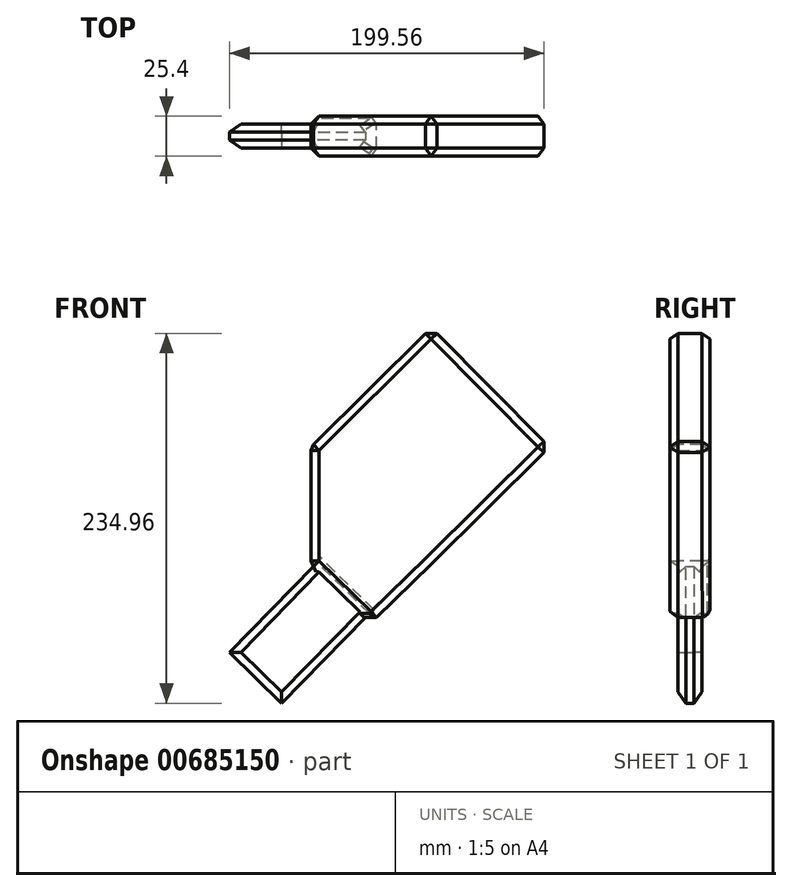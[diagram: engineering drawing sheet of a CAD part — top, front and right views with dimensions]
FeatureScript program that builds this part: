
annotation { "Feature Type Name" : "Feature", "Feature Type Description" : "" }
export const myFeature = defineFeature(function(context is Context, id is Id, definition is map)
    precondition{}
    {
        {
            var Q0;
            Q0=qCreatedBy(makeId("Front.planeOp"),FACE);
            var sketch = newSketch(context, id + "F0", { "sketchPlane" : qUnion([Q0])});
            skLineSegment(sketch, "E0", {"start": v(-76.34, 0) * mm, "end": v(0, 75.72) * mm});
            skLineSegment(sketch, "E1", {"start": v(0, 75.72) * mm, "end": v(75.1, 0) * mm});
            skLineSegment(sketch, "E2", {"start": v(75.1, 0) * mm, "end": v(0, -74.5) * mm});
            skLineSegment(sketch, "E3", {"start": v(0, -74.5) * mm, "end": v(-76.34, 0) * mm});
            skLineSegment(sketch, "E4", {"start": v(-76.34, 0) * mm, "end": v(-76.34, -74.5) * mm});
            skLineSegment(sketch, "E5", {"start": v(-76.34, -74.5) * mm, "end": v(-38.17, -111.74) * mm});
            skPoint(sketch, "E5.endSnap0", {"position": v(-38.17, -37.25) * mm});
            skLineSegment(sketch, "E6", {"start": v(-38.17, -111.74) * mm, "end": v(0, -74.5) * mm});
            skSolve(sketch);
        }
        {
            var Q0;
            Q0=makeQuery(id+"F0.imprint","IMPRINT",FACE,{"disambiguationData":[TD([[makeQuery(id+"F0.imprint","IMPRINT",EDGE,{"derivedFrom":sQuery(id+"F0.wireOp",EDGE,"E0")}),-1.0]])]});
            var Q1;
            Q1=makeQuery(id+"F0.imprint","IMPRINT",FACE,{"disambiguationData":[TD([[makeQuery(id+"F0.imprint","IMPRINT",EDGE,{"derivedFrom":sQuery(id+"F0.wireOp",EDGE,"E3")}),1.0]])]});
            extrude(context, id + "F1", {"entities" : qUnion([Q0, Q1]), "depth" : 25.4 * mm, "offsetDistance" : 25.4 * mm});
        }
        {
            var Q0;
            Q0=makeQuery(id+"F1.opExtrude","CAP_EDGE",EDGE,{"disambiguationData":[OSD([sQuery(id+"F0.wireOp",EDGE,"E2")])],"isStart":false});
            var Q1;
            Q1=makeQuery(id+"F1.opExtrude","CAP_EDGE",EDGE,{"disambiguationData":[OSD([sQuery(id+"F0.wireOp",EDGE,"E5")])],"isStart":false});
            var Q2;
            Q2=makeQuery(id+"F1.opExtrude","CAP_EDGE",EDGE,{"disambiguationData":[OSD([sQuery(id+"F0.wireOp",EDGE,"E4")])],"isStart":false});
            var Q3;
            Q3=makeQuery(id+"F1.opExtrude","CAP_FACE",FACE,{"disambiguationData":[OSD([sQuery(id+"F0.wireOp",EDGE,"E0"),sQuery(id+"F0.wireOp",EDGE,"E1"),sQuery(id+"F0.wireOp",EDGE,"E2"),sQuery(id+"F0.wireOp",EDGE,"E4"),sQuery(id+"F0.wireOp",EDGE,"E5"),sQuery(id+"F0.wireOp",EDGE,"E6")])],"isStart":false});
            var Q4;
            Q4=makeQuery(id+"F1.opExtrude","CAP_EDGE",EDGE,{"disambiguationData":[OSD([sQuery(id+"F0.wireOp",EDGE,"E2")])],"isStart":true});
            var Q5;
            Q5=makeQuery(id+"F1.opExtrude","CAP_EDGE",EDGE,{"disambiguationData":[OSD([sQuery(id+"F0.wireOp",EDGE,"E1")])],"isStart":true});
            var Q6;
            Q6=makeQuery(id+"F1.opExtrude","SWEPT_EDGE",EDGE,{"disambiguationData":[OSD([sQuery(id+"F0.wireOp",EDGE,"E1"),sQuery(id+"F0.wireOp",EDGE,"E2")])]});
            var Q7;
            Q7=makeQuery(id+"F1.opExtrude","SWEPT_EDGE",EDGE,{"disambiguationData":[OSD([sQuery(id+"F0.wireOp",EDGE,"E0"),sQuery(id+"F0.wireOp",EDGE,"E1")])]});
            var Q8;
            Q8=makeQuery(id+"F1.opExtrude","SWEPT_EDGE",EDGE,{"disambiguationData":[OSD([sQuery(id+"F0.wireOp",EDGE,"E5"),sQuery(id+"F0.wireOp",EDGE,"E6")])]});
            var Q9;
            Q9=makeQuery(id+"F1.opExtrude","SWEPT_EDGE",EDGE,{"disambiguationData":[OSD([sQuery(id+"F0.wireOp",EDGE,"E4"),sQuery(id+"F0.wireOp",EDGE,"E5")])]});
            var Q10;
            Q10=makeQuery(id+"F1.opExtrude","SWEPT_EDGE",EDGE,{"disambiguationData":[OSD([sQuery(id+"F0.wireOp",EDGE,"E0"),sQuery(id+"F0.wireOp",EDGE,"E3"),sQuery(id+"F0.wireOp",EDGE,"E4")])]});
            var Q11;
            Q11=makeQuery(id+"F1.opExtrude","CAP_EDGE",EDGE,{"disambiguationData":[OSD([sQuery(id+"F0.wireOp",EDGE,"E4")])],"isStart":true});
            var Q12;
            Q12=makeQuery(id+"F1.opExtrude","CAP_EDGE",EDGE,{"disambiguationData":[OSD([sQuery(id+"F0.wireOp",EDGE,"E5")])],"isStart":true});
            var Q13;
            Q13=makeQuery(id+"F1.opExtrude","CAP_EDGE",EDGE,{"disambiguationData":[OSD([sQuery(id+"F0.wireOp",EDGE,"E0")])],"isStart":true});
            chamfer(context, id + "F2", {"entities" : qUnion([Q0, Q1, Q2, Q3, Q4, Q5, Q6, Q7, Q8, Q9, Q10, Q11, Q12, Q13]), "width" : 5.08 * mm, "tangentPropagation" : true});
        }
        {
            var Q0;
            Q0=makeQuery(id+"F1.opExtrude","SWEPT_FACE",FACE,{"disambiguationData":[OSD([sQuery(id+"F0.wireOp",EDGE,"E5")])]});
            extrude(context, id + "F3", {"entities" : qUnion([Q0]), "operationType" : NewBodyOperationType.ADD, "depth" : 76.2 * mm, "offsetDistance" : 25.4 * mm});
        }
        {
            var Q0;
            {var subQ0=sQuery(id+"F0.wireOp",EDGE,"E5");var subQ1=sQuery(id+"F0.wireOp",EDGE,"E6");Q0=makeQuery(id+"F3.opExtrude","SWEPT_EDGE",EDGE,{"disambiguationData":[OSD([subQ0,subQ1]),TDD([makeQuery(id+"F2.opChamfer","BLEND_VERTEX",VERTEX,{"blendedFrom":[makeQuery(id+"F1.opExtrude","CAP_VERTEX",VERTEX,{"disambiguationData":[OSD([subQ0,subQ1])],"isStart":false}),makeQuery(id+"F1.opExtrude","SWEPT_EDGE",EDGE,{"disambiguationData":[OSD([subQ0,subQ1])]}),makeQuery(id+"F1.opExtrude","CAP_EDGE",EDGE,{"disambiguationData":[OSD([subQ0])],"isStart":false}),makeQuery(id+"F1.opExtrude","SWEPT_FACE",FACE,{"disambiguationData":[OSD([subQ0])]})],"blendedInto":[makeQuery(id+"F1.opExtrude","SWEPT_FACE",FACE,{"disambiguationData":[OSD([subQ0])]})]})])]});}
            var Q1;
            {var subQ0=sQuery(id+"F0.wireOp",EDGE,"E5");var subQ1=sQuery(id+"F0.wireOp",EDGE,"E6");Q1=makeQuery(id+"F3.opExtrude","SWEPT_EDGE",EDGE,{"disambiguationData":[OSD([subQ0,subQ1]),TDD([makeQuery(id+"F2.opChamfer","BLEND_VERTEX",VERTEX,{"blendedFrom":[makeQuery(id+"F1.opExtrude","SWEPT_EDGE",EDGE,{"disambiguationData":[OSD([subQ0,subQ1])]}),makeQuery(id+"F1.opExtrude","CAP_EDGE",EDGE,{"disambiguationData":[OSD([subQ0])],"isStart":true}),makeQuery(id+"F1.opExtrude","SWEPT_FACE",FACE,{"disambiguationData":[OSD([subQ0])]})],"blendedInto":[makeQuery(id+"F1.opExtrude","SWEPT_FACE",FACE,{"disambiguationData":[OSD([subQ0])]})]})])]});}
            var Q2;
            {var subQ0=sQuery(id+"F0.wireOp",EDGE,"E5");Q2=makeQuery(id+"F2.opChamfer","BLEND_EDGE",EDGE,{"blendedFrom":[makeQuery(id+"F1.opExtrude","CAP_EDGE",EDGE,{"disambiguationData":[OSD([subQ0])],"isStart":true}),makeQuery(id+"F1.opExtrude","CAP_FACE",FACE,{"disambiguationData":[OSD([sQuery(id+"F0.wireOp",EDGE,"E0"),sQuery(id+"F0.wireOp",EDGE,"E1"),sQuery(id+"F0.wireOp",EDGE,"E2"),sQuery(id+"F0.wireOp",EDGE,"E4"),subQ0,sQuery(id+"F0.wireOp",EDGE,"E6")])],"isStart":true})],"blendedInto":[makeQuery(id+"F1.opExtrude","CAP_FACE",FACE,{"disambiguationData":[OSD([sQuery(id+"F0.wireOp",EDGE,"E0"),sQuery(id+"F0.wireOp",EDGE,"E1"),sQuery(id+"F0.wireOp",EDGE,"E2"),sQuery(id+"F0.wireOp",EDGE,"E4"),subQ0,sQuery(id+"F0.wireOp",EDGE,"E6")])],"isStart":true})]});}
            var Q3;
            {var subQ0=sQuery(id+"F0.wireOp",EDGE,"E5");Q3=makeQuery(id+"F3.opExtrude","CAP_EDGE",EDGE,{"disambiguationData":[OSD([subQ0]),TDD([makeQuery(id+"F2.opChamfer","BLEND_EDGE",EDGE,{"blendedFrom":[makeQuery(id+"F1.opExtrude","CAP_EDGE",EDGE,{"disambiguationData":[OSD([subQ0])],"isStart":false}),makeQuery(id+"F1.opExtrude","SWEPT_FACE",FACE,{"disambiguationData":[OSD([subQ0])]})],"blendedInto":[makeQuery(id+"F1.opExtrude","SWEPT_FACE",FACE,{"disambiguationData":[OSD([subQ0])]})]})])],"isStart":false});}
            var Q4;
            {var subQ0=sQuery(id+"F0.wireOp",EDGE,"E5");var subQ1=sQuery(id+"F0.wireOp",EDGE,"E4");Q4=makeQuery(id+"F3.opExtrude","SWEPT_EDGE",EDGE,{"disambiguationData":[OSD([subQ1,subQ0]),TDD([makeQuery(id+"F2.opChamfer","BLEND_VERTEX",VERTEX,{"blendedFrom":[makeQuery(id+"F1.opExtrude","CAP_VERTEX",VERTEX,{"disambiguationData":[OSD([subQ1,subQ0])],"isStart":true}),makeQuery(id+"F1.opExtrude","SWEPT_EDGE",EDGE,{"disambiguationData":[OSD([subQ1,subQ0])]}),makeQuery(id+"F1.opExtrude","CAP_EDGE",EDGE,{"disambiguationData":[OSD([subQ0])],"isStart":true}),makeQuery(id+"F1.opExtrude","SWEPT_FACE",FACE,{"disambiguationData":[OSD([subQ0])]})],"blendedInto":[makeQuery(id+"F1.opExtrude","SWEPT_FACE",FACE,{"disambiguationData":[OSD([subQ0])]})]})])]});}
            var Q5;
            {var subQ0=sQuery(id+"F0.wireOp",EDGE,"E5");var subQ1=sQuery(id+"F0.wireOp",EDGE,"E4");Q5=makeQuery(id+"F3.opExtrude","SWEPT_EDGE",EDGE,{"disambiguationData":[OSD([subQ1,subQ0]),TDD([makeQuery(id+"F2.opChamfer","BLEND_VERTEX",VERTEX,{"blendedFrom":[makeQuery(id+"F1.opExtrude","CAP_VERTEX",VERTEX,{"disambiguationData":[OSD([subQ1,subQ0])],"isStart":false}),makeQuery(id+"F1.opExtrude","SWEPT_EDGE",EDGE,{"disambiguationData":[OSD([subQ1,subQ0])]}),makeQuery(id+"F1.opExtrude","CAP_EDGE",EDGE,{"disambiguationData":[OSD([subQ0])],"isStart":false}),makeQuery(id+"F1.opExtrude","SWEPT_FACE",FACE,{"disambiguationData":[OSD([subQ0])]})],"blendedInto":[makeQuery(id+"F1.opExtrude","SWEPT_FACE",FACE,{"disambiguationData":[OSD([subQ0])]})]})])]});}
            chamfer(context, id + "F4", {"entities" : qUnion([Q0, Q1, Q2, Q3, Q4, Q5]), "width" : 5.08 * mm, "tangentPropagation" : true});
        }
        {
            var Q0;
            {var subQ0=sQuery(id+"F0.wireOp",EDGE,"E5");Q0=makeQuery(id+"F3.opExtrude","CAP_EDGE",EDGE,{"disambiguationData":[OSD([subQ0]),TDD([makeQuery(id+"F2.opChamfer","BLEND_EDGE",EDGE,{"blendedFrom":[makeQuery(id+"F1.opExtrude","CAP_EDGE",EDGE,{"disambiguationData":[OSD([subQ0])],"isStart":true}),makeQuery(id+"F1.opExtrude","SWEPT_FACE",FACE,{"disambiguationData":[OSD([subQ0])]})],"blendedInto":[makeQuery(id+"F1.opExtrude","SWEPT_FACE",FACE,{"disambiguationData":[OSD([subQ0])]})]})])],"isStart":false});}
            chamfer(context, id + "F5", {"entities" : qUnion([Q0]), "width" : 5.08 * mm, "tangentPropagation" : true});
        }
        {
            var Q0;
            {var subQ0=sQuery(id+"F0.wireOp",EDGE,"E5");Q0=makeQuery(id+"F2.opChamfer","BLEND_EDGE",EDGE,{"blendedFrom":[makeQuery(id+"F1.opExtrude","SWEPT_EDGE",EDGE,{"disambiguationData":[OSD([subQ0,sQuery(id+"F0.wireOp",EDGE,"E6")])]}),makeQuery(id+"F1.opExtrude","CAP_EDGE",EDGE,{"disambiguationData":[OSD([subQ0])],"isStart":true})],"blendedInto":[]});}
            var Q1;
            {var subQ0=sQuery(id+"F0.wireOp",EDGE,"E5");var subQ1=sQuery(id+"F0.wireOp",EDGE,"E6");var subQ2=makeQuery(id+"F2.opChamfer","BLEND_VERTEX",VERTEX,{"blendedFrom":[makeQuery(id+"F1.opExtrude","CAP_VERTEX",VERTEX,{"disambiguationData":[OSD([subQ0,subQ1])],"isStart":false}),makeQuery(id+"F1.opExtrude","SWEPT_EDGE",EDGE,{"disambiguationData":[OSD([subQ0,subQ1])]}),makeQuery(id+"F1.opExtrude","CAP_EDGE",EDGE,{"disambiguationData":[OSD([subQ0])],"isStart":false}),makeQuery(id+"F1.opExtrude","SWEPT_FACE",FACE,{"disambiguationData":[OSD([subQ0])]})],"blendedInto":[makeQuery(id+"F1.opExtrude","SWEPT_FACE",FACE,{"disambiguationData":[OSD([subQ0])]})]});Q1=makeQuery(id+"F4.opChamfer","TWEAK_EDGE",EDGE,{"derivedFrom":[makeQuery(id+"F3.boolean.opBoolean","MERGE",VERTEX,{"derivedFrom":[subQ2,makeQuery(id+"F3.opExtrude","CAP_VERTEX",VERTEX,{"disambiguationData":[OSD([subQ0,subQ1]),TDD([subQ2])],"isStart":true})]})]});}
            chamfer(context, id + "F6", {"entities" : qUnion([Q0, Q1]), "width" : 5.08 * mm, "tangentPropagation" : true});
        }
    });
